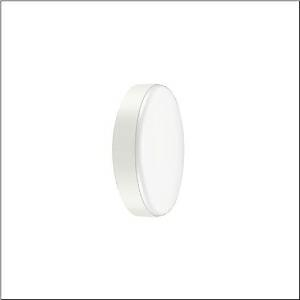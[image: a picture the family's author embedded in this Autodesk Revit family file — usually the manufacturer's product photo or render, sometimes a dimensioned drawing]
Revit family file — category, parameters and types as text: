
# Revit family: round_31_51wc10ma32a
name_source: partatom
category: Lighting Fixtures
units: mm (PartAtom-declared; Revit-internal decimal feet)

## family parameters
Cut with Voids When Loaded = No
Host = Face
Light Source = No
Part Type = Normal
Room Calculation Point = No
Round Connector Dimension = Use Diameter
Shared = No

## types (1)
- --- (1 x LED, 2450 lm, 19 W, 3000K)
    Apparent Load = 19 VA
    CIE Flux Codes = 44 75 94 94 100
    Color Rendering = 80
    Color Temperature = 3000K
    Default Elevation = 1800 mm
    Description = Round 31, wall and ceiling luminaire, primary optical cover: cover, of PC, opal, light emission: direct distribution, primary light characteristic: symmetric, installation type: surface-mounted, LED, rated luminous flux: 2.450lm, luminous efficacy: 129lm/W, light colour: 830, colour temperature: 3000K, control gear: ON/OFF Multilumen, with terminal, 3-pole, max. 2.5mm², mains connection: 220..240V, AC, 50/60Hz, rated input power: 19W, luminaire housing, of PC, traffic white (RAL 9016), diameter: 350mm, protection rating (complete): IP65, insulation class (complete): insulation class II (safety insulation), certification: CE, impact resistance: IK10, permissible operating ambient temperature: -20..+40°C, permissible storage temperature: -20..+60°C, packaging unit: 1 piece
    Height = 97 mm
    Lamp = 1 x LED
    Lamp Light Flux = 2450 lm
    Lamp Power = 19 W
    Lamp count = 1
    Length = 350 mm
    Luminous efficacy = 129 lm/W
    Manufacturer = Siteco
    ModVariant = No
    Model = 51WC10MA32A
    Mounting Place = Ceiling
    Mounting Type = Surface mounted
    Number of Poles = 1
    OnlyDefault = Yes
    Power Factor = 1
    Product Name = Round 31
    Product group = wall and ceiling luminaire | ceiling mounted
    ProductGroupID = 305
    Protection Class = Protection class II
    Protection Degree = IP 65
    RLX_Detail_Level = 1
    RLX_Emergency_Light_Flux = 0 lm
    RLX_Emergency_Type = 0
    RLX_Emergency_Type_DB = No
    RlxData = <blob elided: 31745 chars, md5=33c2f084>
    Socket = socket
    Standby Power = 0 W
    System Light Flux = 2450 lm
    System Power = 19 W
    Type Comments = factory setting: luminous flux: 100 % | (ON | ON)
    Type Image = l_1007027.jpg
    URL = http://relux.com
    VarID = @adj_172353
    Voltage = 0 V
    Weight = 0.00 kg
    Width = 0 mm  [stored 0 ft]

note: [stored X ft] marks values corroborated as IEEE doubles in the binary element streams (Revit-internal decimal feet)

## geometry (parser evidence)
native form markers: Blend x4, Sweep x12
no freeform markers — native parametric forms only
